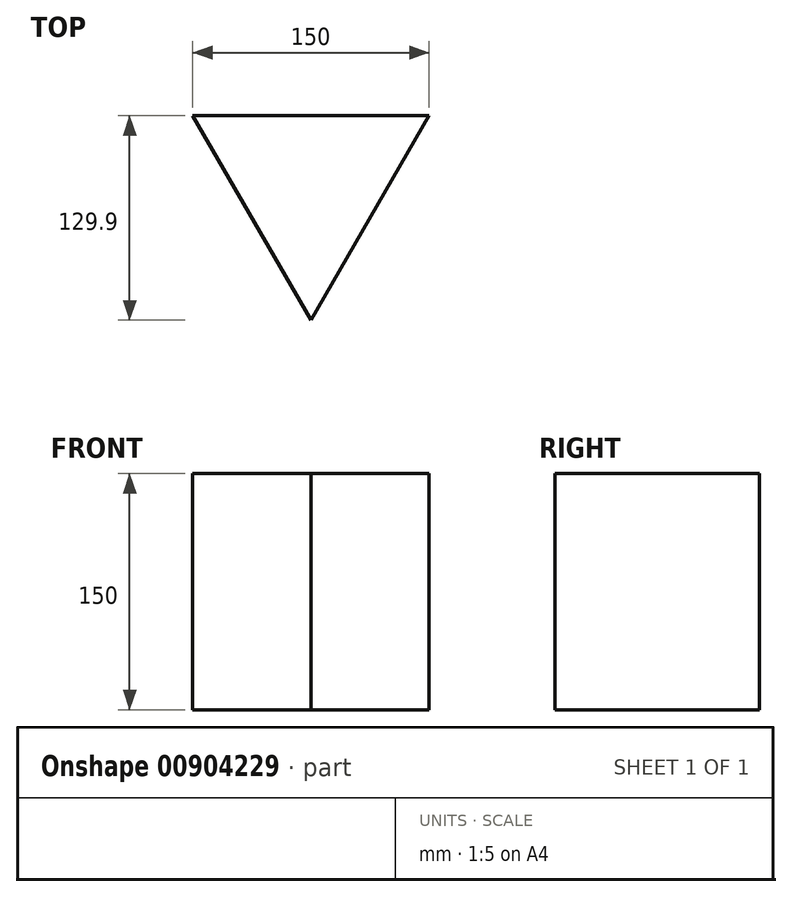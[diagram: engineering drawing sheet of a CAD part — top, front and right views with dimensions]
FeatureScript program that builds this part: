
annotation { "Feature Type Name" : "Feature", "Feature Type Description" : "" }
export const myFeature = defineFeature(function(context is Context, id is Id, definition is map)
    precondition{}
    {
        {
            var Q0;
            Q0=qCreatedBy(makeId("Top.planeOp"),FACE);
            var sketch = newSketch(context, id + "F0", { "sketchPlane" : qUnion([Q0])});
            skCircle(sketch, "E0.cCircle", {"center": v(0, 0) * mm, "radius": 43.3 * mm, "construction": true});
            skLineSegment(sketch, "E0.0", {"start": v(-75, 43.3) * mm, "end": v(75, 43.3) * mm});
            skLineSegment(sketch, "E0.1", {"start": v(75, 43.3) * mm, "end": v(0, -86.6) * mm});
            skLineSegment(sketch, "E0.2", {"start": v(0, -86.6) * mm, "end": v(-75, 43.3) * mm});
            skPoint(sketch, "E0.0.midPoint", {"position": v(0, 43.3) * mm});
            skSolve(sketch);
        }
        {
            var Q0;
            Q0=makeQuery(id+"F0.imprint","IMPRINT",FACE,{"disambiguationData":[TD([[makeQuery(id+"F0.imprint","IMPRINT",EDGE,{"derivedFrom":sQuery(id+"F0.wireOp",EDGE,"E0.0")}),-1.0]])]});
            extrude(context, id + "F1", {"entities" : qUnion([Q0]), "depth" : 150 * mm, "offsetDistance" : 25 * mm});
        }
    });
